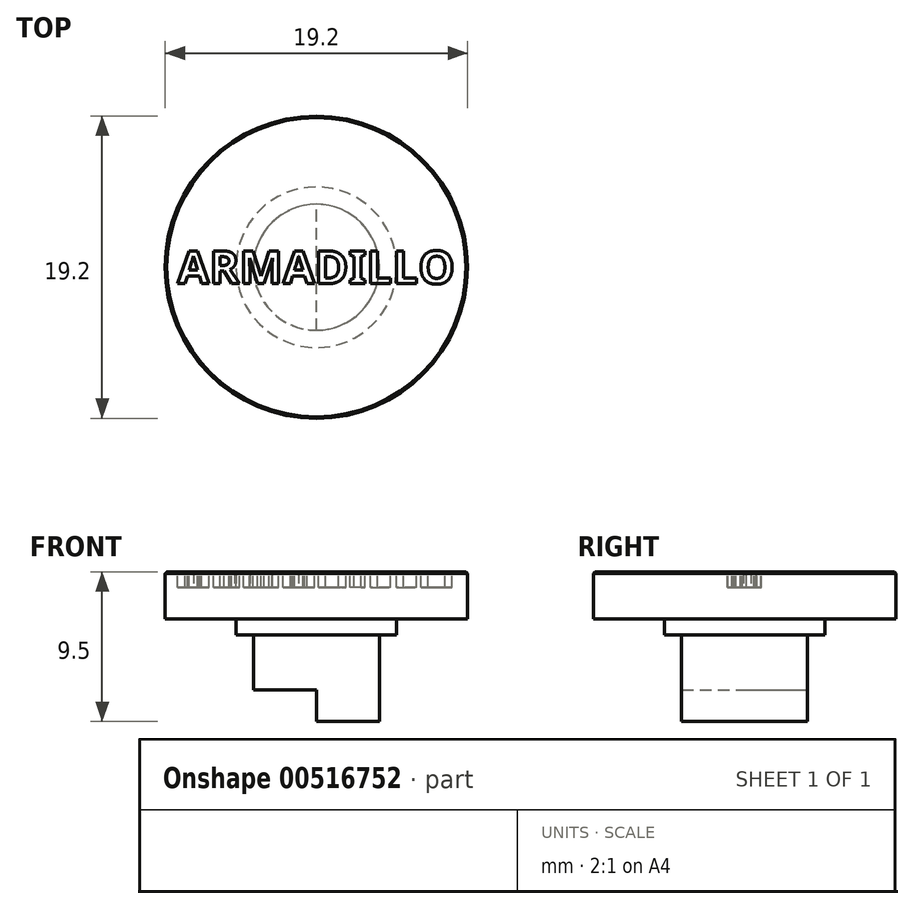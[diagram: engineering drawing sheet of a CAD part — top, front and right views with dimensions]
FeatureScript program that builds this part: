
annotation { "Feature Type Name" : "Feature", "Feature Type Description" : "" }
export const myFeature = defineFeature(function(context is Context, id is Id, definition is map)
    precondition{}
    {
        {
            var Q0;
            Q0=qCreatedBy(makeId("Front.planeOp"),FACE);
            var sketch = newSketch(context, id + "F0", { "sketchPlane" : qUnion([Q0])});
            skLineSegment(sketch, "E0", {"start": v(0, 0) * mm, "end": v(0, 9.5) * mm});
            skLineSegment(sketch, "E1", {"start": v(0, 9.5) * mm, "end": v(9.6, 9.5) * mm});
            skLineSegment(sketch, "E2", {"start": v(9.6, 9.5) * mm, "end": v(9.6, 6.5) * mm});
            skLineSegment(sketch, "E3", {"start": v(9.6, 6.5) * mm, "end": v(5.1, 6.5) * mm});
            skLineSegment(sketch, "E4", {"start": v(5.1, 6.5) * mm, "end": v(5.1, 5.5) * mm});
            skLineSegment(sketch, "E5", {"start": v(5.1, 5.5) * mm, "end": v(4, 5.5) * mm});
            skLineSegment(sketch, "E6", {"start": v(4, 5.5) * mm, "end": v(4, 0) * mm});
            skLineSegment(sketch, "E7", {"start": v(4, 0) * mm, "end": v(0, 0) * mm});
            skSolve(sketch);
        }
        {
            var Q0;
            Q0=makeQuery(id+"F0.imprint","IMPRINT",FACE,{"disambiguationData":[TD([[makeQuery(id+"F0.imprint","IMPRINT",EDGE,{"derivedFrom":sQuery(id+"F0.wireOp",EDGE,"E0")}),-1.0]])]});
            var Q1;
            Q1=sQuery(id+"F0.wireOp",EDGE,"E0");
            revolve(context, id + "F1", {"entities" : qUnion([Q0]), "axis" : qUnion([Q1]), "revolveType" : RevolveType.FULL});
        }
        {
            var Q0;
            Q0=makeQuery(id+"F1.opRevolve","SWEPT_FACE",FACE,{"disambiguationData":[OSD([sQuery(id+"F0.wireOp",EDGE,"E7")])]});
            var sketch = newSketch(context, id + "F2", { "sketchPlane" : qUnion([Q0])});
            skArc(sketch, "E8", {"start": v(0, 4) * mm, "mid": v(-4, 0) * mm, "end": v(0, -4) * mm});
            skLineSegment(sketch, "E9", {"start": v(0, 4) * mm, "end": v(0, -4) * mm});
            skSolve(sketch);
        }
        {
            var Q0;
            Q0=makeQuery(id+"F2.imprint","IMPRINT",FACE,{"disambiguationData":[TD([[makeQuery(id+"F2.imprint","IMPRINT",EDGE,{"derivedFrom":sQuery(id+"F2.wireOp",EDGE,"E8")}),1.0]])]});
            extrude(context, id + "F3", {"entities" : qUnion([Q0]), "operationType" : NewBodyOperationType.REMOVE, "oppositeDirection" : true, "depth" : 2 * mm, "offsetDistance" : 25 * mm});
        }
        {
            var Q0;
            Q0=makeQuery(id+"F1.opRevolve","SWEPT_EDGE",EDGE,{"disambiguationData":[OSD([sQuery(id+"F0.wireOp",EDGE,"E1"),sQuery(id+"F0.wireOp",EDGE,"E2")])]});
            chamfer(context, id + "F4", {"entities" : qUnion([Q0]), "width" : 0.1 * mm, "tangentPropagation" : true});
        }
        {
            var Q0;
            Q0=makeQuery(id+"F1.opRevolve","SWEPT_FACE",FACE,{"disambiguationData":[OSD([sQuery(id+"F0.wireOp",EDGE,"E1")])]});
            var sketch = newSketch(context, id + "F5", { "sketchPlane" : qUnion([Q0])});
            skText(sketch, "E10", { "text": "ARMADILLO", "fontName": "NotoSans-Bold.ttf"});
            skPoint(sketch, "E11", {"position": v(0, 0) * mm});
            const initialGuessF5  = {"E10": [-0.00882, -0.00105, 1, 0, 0.0021]};
            skSetInitialGuess(sketch, initialGuessF5);
            skSolve(sketch);
        }
        {
            var Q0;
            Q0 = qSketchRegion(id + "F5", true);
            extrude(context, id + "F6", {"entities" : qUnion([Q0]), "operationType" : NewBodyOperationType.REMOVE, "oppositeDirection" : true, "depth" : 1 * mm, "offsetDistance" : 25 * mm});
        }
    });
